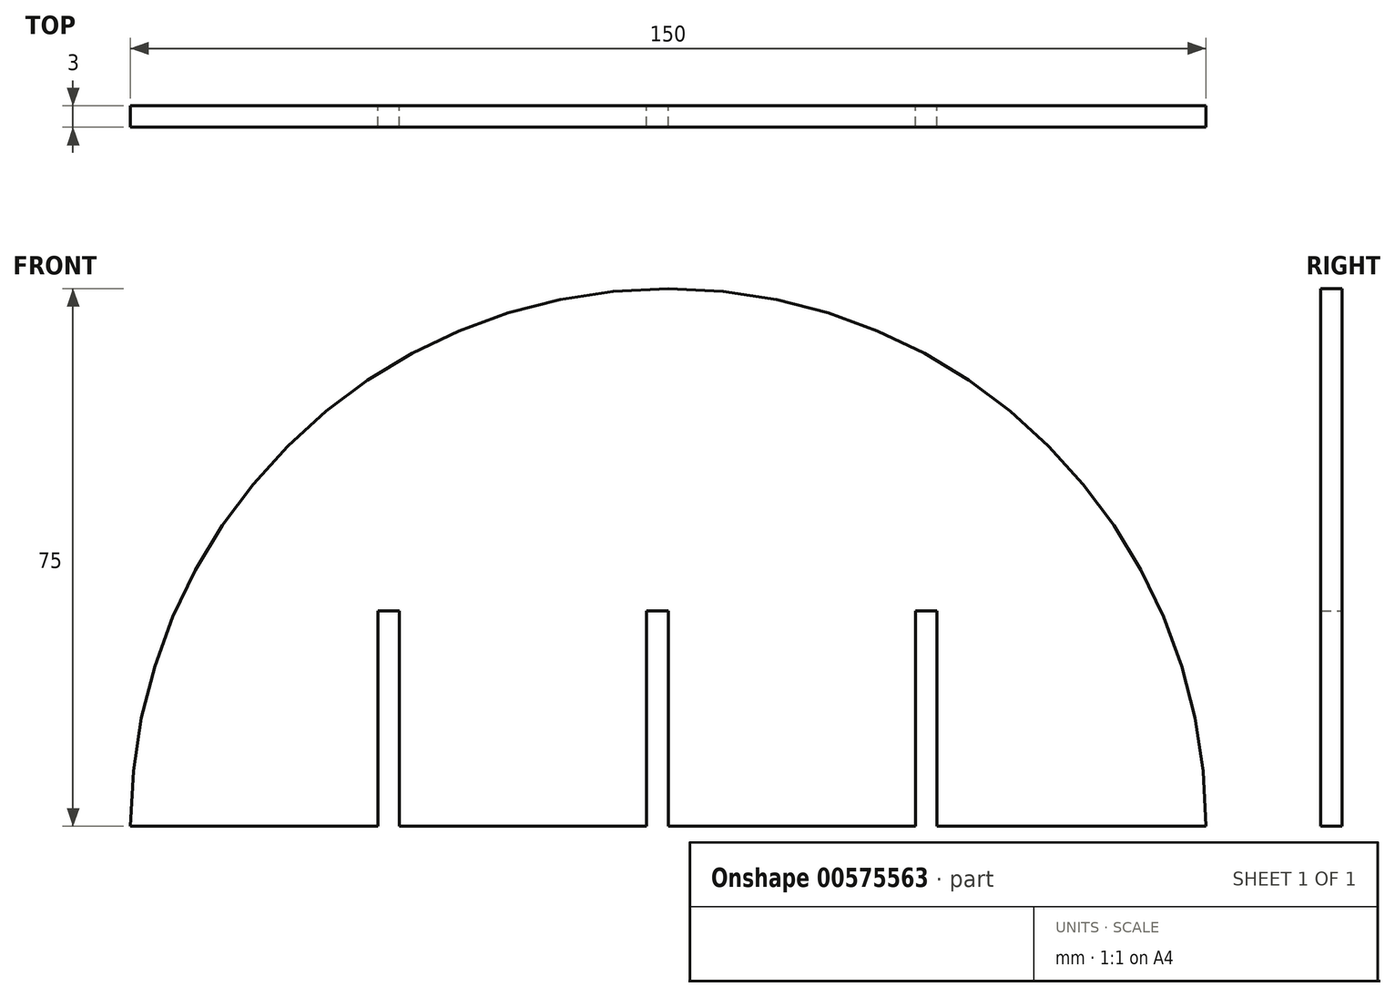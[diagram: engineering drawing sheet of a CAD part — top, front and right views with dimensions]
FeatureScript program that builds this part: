
annotation { "Feature Type Name" : "Feature", "Feature Type Description" : "" }
export const myFeature = defineFeature(function(context is Context, id is Id, definition is map)
    precondition{}
    {
        {
            var Q0;
            Q0=qCreatedBy(makeId("Front.planeOp"),FACE);
            var sketch = newSketch(context, id + "F0", { "sketchPlane" : qUnion([Q0])});
            skPoint(sketch, "E0.end.orphan", {"position": v(-75, 0) * mm});
            skPoint(sketch, "E1.start.orphan", {"position": v(75, 0) * mm});
            skLineSegment(sketch, "E2", {"start": v(75, 0) * mm, "end": v(37.5, 0) * mm});
            skArc(sketch, "E3", {"start": v(-75, 0) * mm, "mid": v(0, 75) * mm, "end": v(75, 0) * mm});
            skLineSegment(sketch, "E4", {"start": v(-75, 0) * mm, "end": v(-40.5, 0) * mm});
            skLineSegment(sketch, "E5", {"start": v(-37.5, 0) * mm, "end": v(-3, 0) * mm});
            skLineSegment(sketch, "E6", {"start": v(0, 0) * mm, "end": v(34.5, 0) * mm});
            skLineSegment(sketch, "E7", {"start": v(37.5, 0) * mm, "end": v(75, 0) * mm});
            skLineSegment(sketch, "E8", {"start": v(-37.5, 0) * mm, "end": v(-37.5, 30) * mm});
            skLineSegment(sketch, "E9", {"start": v(0, 0) * mm, "end": v(0, 30) * mm});
            skLineSegment(sketch, "E10", {"start": v(37.5, 0) * mm, "end": v(37.5, 30) * mm});
            skPoint(sketch, "E11", {"position": v(-40.5, 0) * mm});
            skPoint(sketch, "E12", {"position": v(-3, 0) * mm});
            skPoint(sketch, "E13", {"position": v(34.5, 0) * mm});
            skLineSegment(sketch, "E14", {"start": v(-40.5, 0) * mm, "end": v(-40.5, 30) * mm});
            skLineSegment(sketch, "E15", {"start": v(-40.5, 30) * mm, "end": v(-37.5, 30) * mm});
            skLineSegment(sketch, "E16", {"start": v(-3, 0) * mm, "end": v(-3, 30) * mm});
            skLineSegment(sketch, "E17", {"start": v(-3, 30) * mm, "end": v(0, 30) * mm});
            skLineSegment(sketch, "E18", {"start": v(34.5, 0) * mm, "end": v(34.5, 30) * mm});
            skLineSegment(sketch, "E19", {"start": v(34.5, 30) * mm, "end": v(37.5, 30) * mm});
            skLineSegment(sketch, "E20.trimOffspring", {"start": v(-40.5, 0) * mm, "end": v(-75, 0) * mm});
            skLineSegment(sketch, "E21.trimOffspring", {"start": v(-3, 0) * mm, "end": v(-37.5, 0) * mm});
            skLineSegment(sketch, "E22.trimOffspring", {"start": v(34.5, 0) * mm, "end": v(0, 0) * mm});
            skSolve(sketch);
        }
        {
            var Q0;
            Q0=qSketchRegion(id+"F0",true);
            extrude(context, id + "F1", {"entities" : qUnion([Q0]), "depth" : 3 * mm, "offsetDistance" : 25 * mm});
        }
    });
